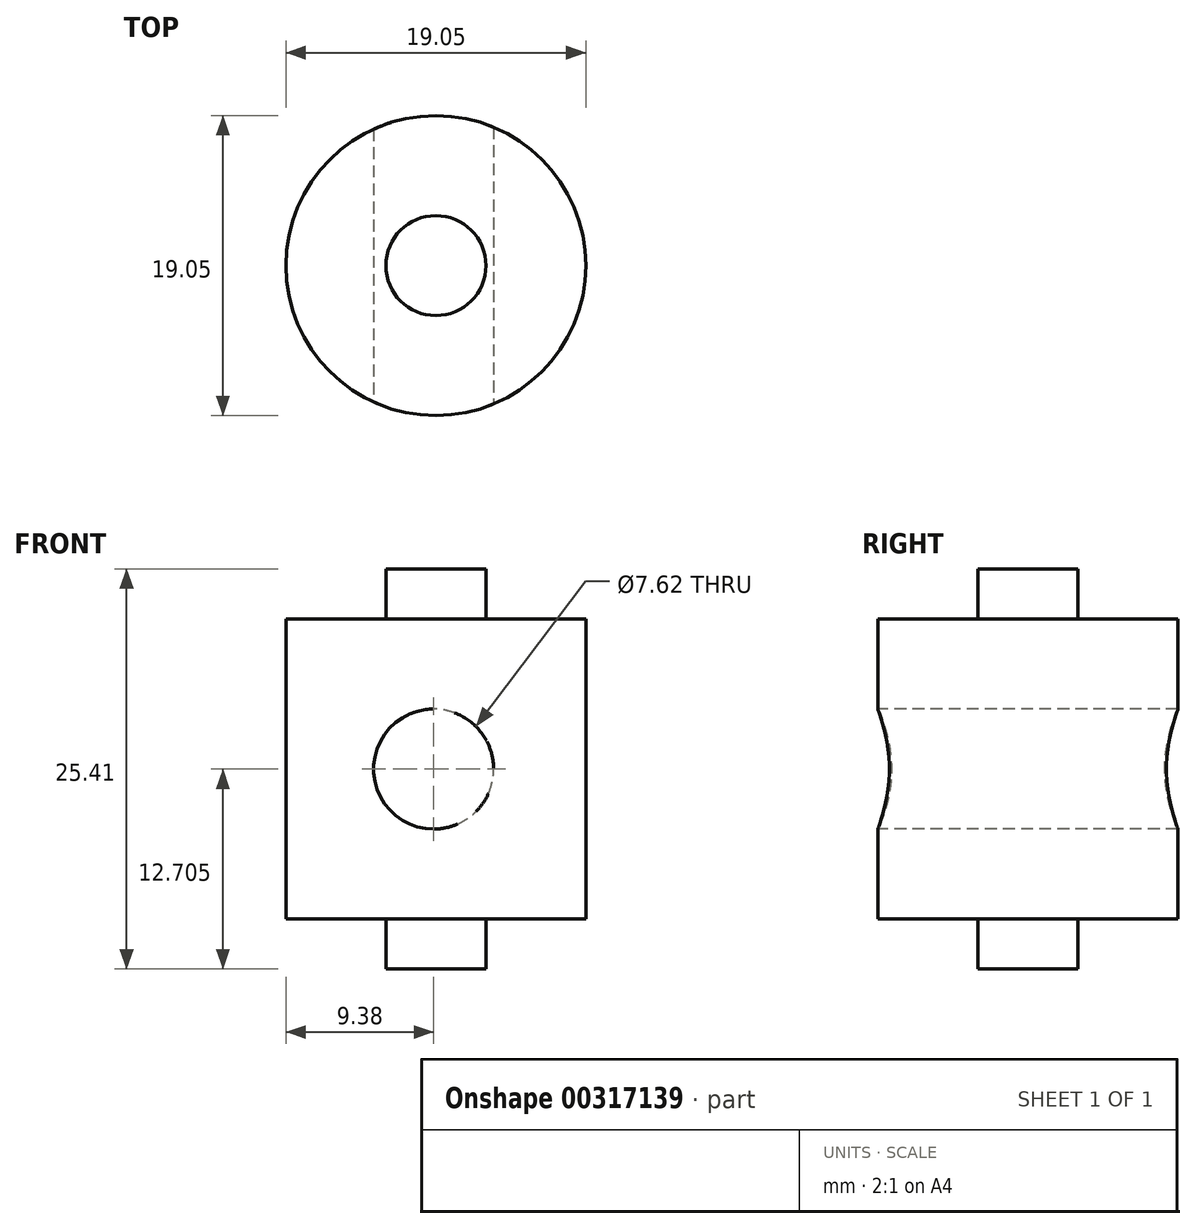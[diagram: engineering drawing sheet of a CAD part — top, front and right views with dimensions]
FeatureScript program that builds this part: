
annotation { "Feature Type Name" : "Feature", "Feature Type Description" : "" }
export const myFeature = defineFeature(function(context is Context, id is Id, definition is map)
    precondition{}
    {
        {
            var Q0;
            Q0=qCreatedBy(makeId("Top.planeOp"),FACE);
            var sketch = newSketch(context, id + "F0", { "sketchPlane" : qUnion([Q0])});
            skCircle(sketch, "E0", {"center": v(0.14, -0.06) * mm, "radius": 9.53 * mm});
            skSolve(sketch);
        }
        {
            var Q0;
            Q0=qSketchRegion(id+"F0",true);
            extrude(context, id + "F1", {"entities" : qUnion([Q0]), "depth" : 19.05 * mm});
        }
        {
            var Q0;
            Q0=makeQuery(id+"F1.opExtrude","CAP_FACE",FACE,{"disambiguationData":[OSD([sQuery(id+"F0.wireOp",EDGE,"E0")])],"isStart":false});
            var sketch = newSketch(context, id + "F2", { "sketchPlane" : qUnion([Q0])});
            skCircle(sketch, "E1", {"center": v(0.14, -0.06) * mm, "radius": 3.18 * mm});
            skSolve(sketch);
        }
        {
            var Q0;
            Q0=qSketchRegion(id+"F2",true);
            extrude(context, id + "F3", {"entities" : qUnion([Q0]), "operationType" : NewBodyOperationType.ADD, "depth" : 3.17 * mm});
        }
        {
            var Q0;
            Q0=makeQuery(id+"F1.opExtrude","CAP_FACE",FACE,{"disambiguationData":[OSD([sQuery(id+"F0.wireOp",EDGE,"E0")])],"isStart":true});
            var sketch = newSketch(context, id + "F4", { "sketchPlane" : qUnion([Q0])});
            skCircle(sketch, "E2", {"center": v(0.14, 0.06) * mm, "radius": 3.18 * mm});
            skSolve(sketch);
        }
        {
            var Q0;
            Q0=qSketchRegion(id+"F4",true);
            extrude(context, id + "F5", {"entities" : qUnion([Q0]), "operationType" : NewBodyOperationType.ADD, "depth" : 3.17 * mm});
        }
        {
            var Q0;
            Q0=qCreatedBy(makeId("Front.planeOp"),FACE);
            var sketch = newSketch(context, id + "F6", { "sketchPlane" : qUnion([Q0])});
            skCircle(sketch, "E3", {"center": v(0, 9.53) * mm, "radius": 3.81 * mm});
            skSolve(sketch);
        }
        {
            var Q0;
            Q0=qSketchRegion(id+"F6",true);
            extrude(context, id + "F7", {"entities" : qUnion([Q0]), "operationType" : NewBodyOperationType.REMOVE, "oppositeDirection" : true, "depth" : 25.4 * mm});
        }
        {
            var Q0;
            Q0=makeQuery(id+"F7.boolean.opBoolean","COPY",FACE,{"derivedFrom":makeQuery(id+"F7.opExtrude","CAP_FACE",FACE,{"disambiguationData":[OSD([sQuery(id+"F6.wireOp",EDGE,"E3")])],"isStart":true})});
            var sketch = newSketch(context, id + "F8", { "sketchPlane" : qUnion([Q0])});
            skCircle(sketch, "E4", {"center": v(0, 9.53) * mm, "radius": 3.81 * mm});
            skSolve(sketch);
        }
        {
            var Q0;
            Q0=qSketchRegion(id+"F8",true);
            extrude(context, id + "F9", {"entities" : qUnion([Q0]), "operationType" : NewBodyOperationType.REMOVE, "oppositeDirection" : true, "depth" : 25.4 * mm});
        }
    });
